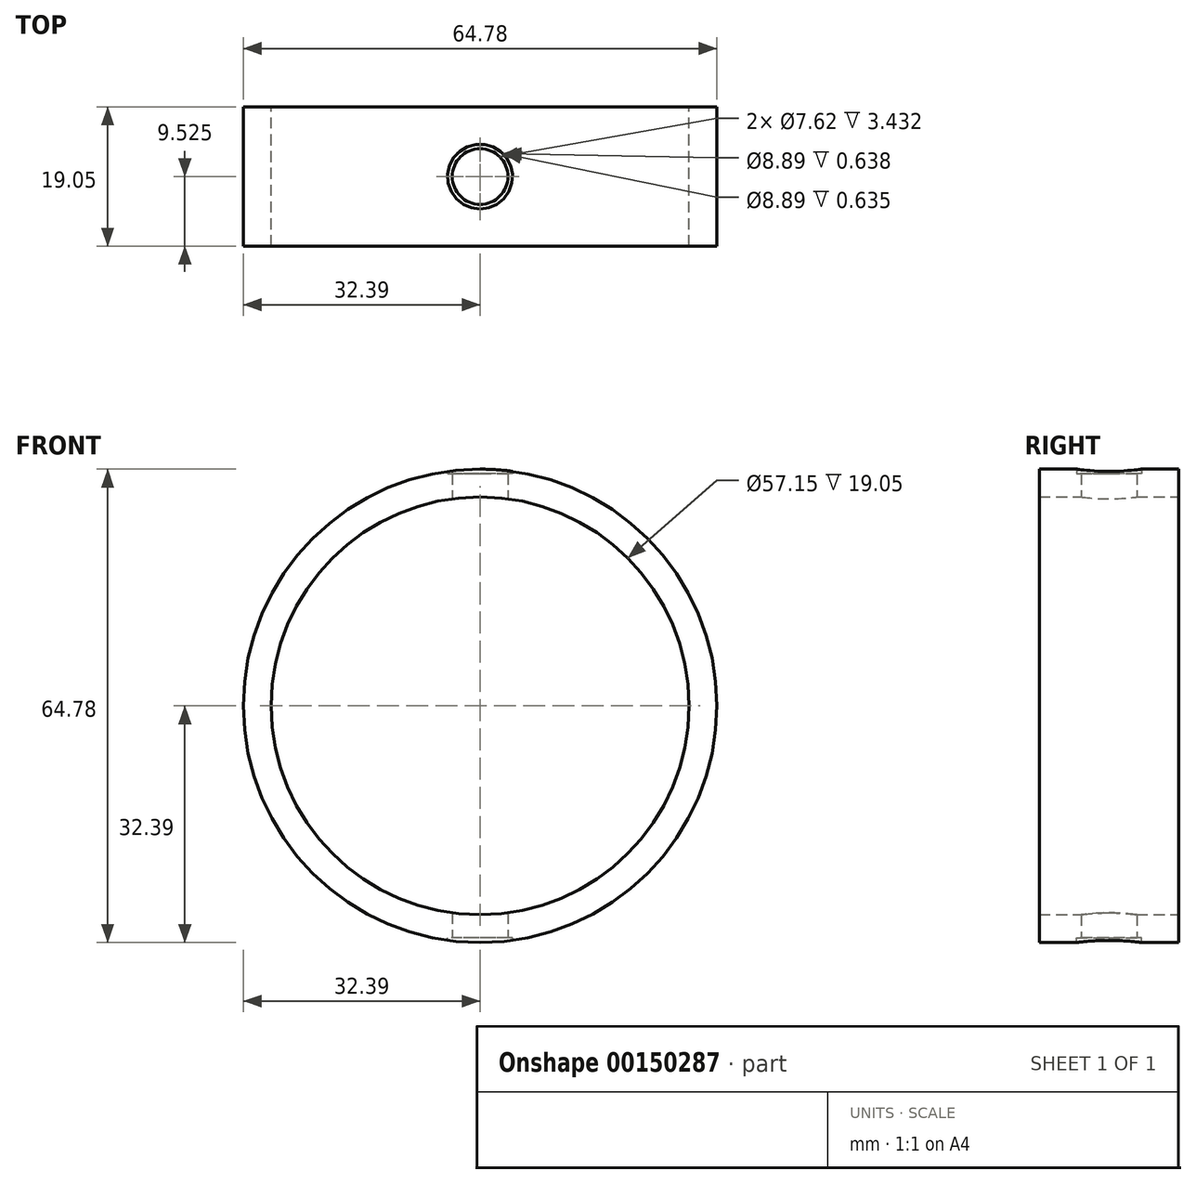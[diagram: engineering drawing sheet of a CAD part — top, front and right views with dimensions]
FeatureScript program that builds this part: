
annotation { "Feature Type Name" : "Feature", "Feature Type Description" : "" }
export const myFeature = defineFeature(function(context is Context, id is Id, definition is map)
    precondition{}
    {
        {
            var Q0;
            Q0=qCreatedBy(makeId("Front.planeOp"),FACE);
            var sketch = newSketch(context, id + "F0", { "sketchPlane" : qUnion([Q0])});
            skCircle(sketch, "E0", {"center": v(0, 0) * mm, "radius": 32.39 * mm});
            skCircle(sketch, "E1", {"center": v(0, 0) * mm, "radius": 28.58 * mm});
            skSolve(sketch);
        }
        {
            var Q0;
            Q0=makeQuery(id+"F0.imprint","IMPRINT",FACE,{"disambiguationData":[TD([[makeQuery(id+"F0.imprint","IMPRINT",EDGE,{"derivedFrom":sQuery(id+"F0.wireOp",EDGE,"E0")}),1.0]])]});
            extrude(context, id + "F1", {"entities" : qUnion([Q0]), "depth" : 19.05 * mm});
        }
        {
            var Q0;
            Q0=qCreatedBy(makeId("Top.planeOp"),FACE);
            var sketch = newSketch(context, id + "F2", { "sketchPlane" : qUnion([Q0])});
            skCircle(sketch, "E2", {"center": v(0, -9.53) * mm, "radius": 3.81 * mm});
            skSolve(sketch);
        }
        {
            var Q0;
            Q0 = qSketchRegion(id + "F2", true);
            extrude(context, id + "F3", {"entities" : qUnion([Q0]), "operationType" : NewBodyOperationType.REMOVE, "endBound" : BoundingType.SYMMETRIC, "depth" : 76.2 * mm});
        }
        {
            var Q0;
            Q0=qCreatedBy(makeId("Top.planeOp"),FACE);
            cPlane(context, id + "F4", {"entities" : qUnion([Q0]), "cplaneType" : CPlaneType.OFFSET, "offset" : 31.75 * mm, "width" : 152.4 * mm, "height" : 152.4 * mm});
        }
        {
            var Q0;
            Q0=qCreatedBy(makeId("Top.planeOp"),FACE);
            cPlane(context, id + "F5", {"entities" : qUnion([Q0]), "cplaneType" : CPlaneType.OFFSET, "offset" : 31.75 * mm, "oppositeDirection" : true, "width" : 152.4 * mm, "height" : 152.4 * mm});
        }
        {
            var Q0;
            Q0=qCreatedBy(id+"F4.planeOp",FACE);
            var sketch = newSketch(context, id + "F6", { "sketchPlane" : qUnion([Q0])});
            skCircle(sketch, "E3", {"center": v(0, -9.53) * mm, "radius": 4.45 * mm});
            skCircle(sketch, "E4.0", {"center": v(0, -9.53) * mm, "radius": 3.81 * mm});
            skSolve(sketch);
        }
        {
            var Q0;
            Q0 = qSketchRegion(id + "F6", true);
            extrude(context, id + "F7", {"entities" : qUnion([Q0]), "operationType" : NewBodyOperationType.REMOVE, "depth" : 25.4 * mm});
        }
        {
            var Q0;
            Q0=qCreatedBy(id+"F5.planeOp",FACE);
            var sketch = newSketch(context, id + "F8", { "sketchPlane" : qUnion([Q0])});
            skCircle(sketch, "E5", {"center": v(0, -9.53) * mm, "radius": 4.45 * mm});
            skCircle(sketch, "E6.0", {"center": v(0, -9.53) * mm, "radius": 3.81 * mm});
            skSolve(sketch);
        }
        {
            var Q0;
            Q0 = qSketchRegion(id + "F8", true);
            extrude(context, id + "F9", {"entities" : qUnion([Q0]), "operationType" : NewBodyOperationType.REMOVE, "oppositeDirection" : true, "depth" : 25.4 * mm});
        }
    });
